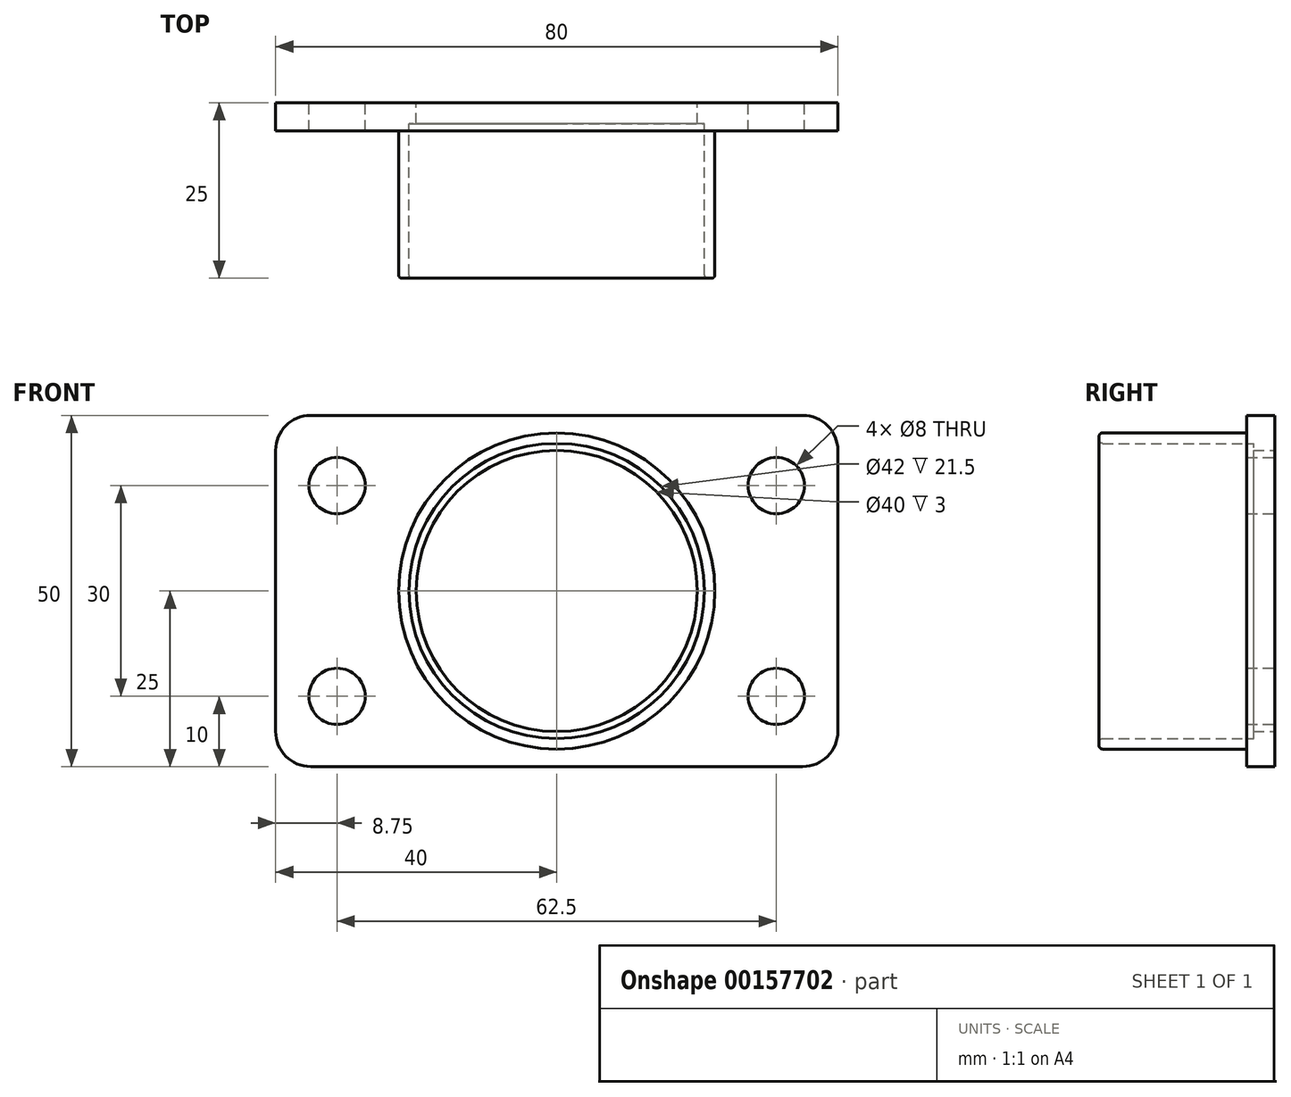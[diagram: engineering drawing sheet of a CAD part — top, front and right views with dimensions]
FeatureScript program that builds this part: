
annotation { "Feature Type Name" : "Feature", "Feature Type Description" : "" }
export const myFeature = defineFeature(function(context is Context, id is Id, definition is map)
    precondition{}
    {
        {
            var Q0;
            Q0=qCreatedBy(makeId("Front.planeOp"),FACE);
            var sketch = newSketch(context, id + "F0", { "sketchPlane" : qUnion([Q0])});
            skLineSegment(sketch, "E0.bottom", {"start": v(-40, 25) * mm, "end": v(40, 25) * mm});
            skLineSegment(sketch, "E0.top", {"start": v(-40, -25) * mm, "end": v(40, -25) * mm});
            skLineSegment(sketch, "E0.left", {"start": v(-40, 25) * mm, "end": v(-40, -25) * mm});
            skLineSegment(sketch, "E0.right", {"start": v(40, 25) * mm, "end": v(40, -25) * mm});
            skPoint(sketch, "E0.middle", {"position": v(0, 0) * mm});
            skCircle(sketch, "E1", {"center": v(0, 0) * mm, "radius": 22.5 * mm});
            skCircle(sketch, "E2", {"center": v(0, 0) * mm, "radius": 21 * mm});
            skLineSegment(sketch, "E3", {"start": v(-40, 0) * mm, "end": v(-31.25, 0) * mm});
            skPoint(sketch, "E3.endSnap0", {"position": v(-40, 0) * mm});
            skLineSegment(sketch, "E4", {"start": v(40, 0) * mm, "end": v(31.25, 0) * mm});
            skLineSegment(sketch, "E5", {"start": v(-31.25, 0) * mm, "end": v(-31.25, 15) * mm});
            skLineSegment(sketch, "E6", {"start": v(-31.25, 0) * mm, "end": v(-31.25, -15) * mm});
            skLineSegment(sketch, "E7", {"start": v(31.25, 0) * mm, "end": v(31.25, 15) * mm});
            skLineSegment(sketch, "E8", {"start": v(31.25, 0) * mm, "end": v(31.25, -15) * mm});
            skCircle(sketch, "E9", {"center": v(-31.25, 15) * mm, "radius": 4 * mm});
            skCircle(sketch, "E10", {"center": v(-31.25, -15) * mm, "radius": 4 * mm});
            skCircle(sketch, "E11", {"center": v(31.25, 15) * mm, "radius": 4 * mm});
            skCircle(sketch, "E12", {"center": v(31.25, -15) * mm, "radius": 4 * mm});
            skCircle(sketch, "E13", {"center": v(0, 0) * mm, "radius": 20 * mm});
            skSolve(sketch);
        }
        {
            var Q0;
            {var subQ3=sQuery(id+"F0.wireOp",EDGE,"E0.bottom");Q0=makeQuery(id+"F0.imprint","IMPRINT",FACE,{"disambiguationData":[TD([[makeQuery(id+"F0.imprint","IMPRINT",EDGE,{"derivedFrom":subQ3}),-1.0]])]});}
            extrude(context, id + "F1", {"entities" : qUnion([Q0]), "depth" : 4 * mm});
        }
        {
            var Q0;
            Q0=makeQuery(id+"F0.imprint","IMPRINT",FACE,{"disambiguationData":[TD([[makeQuery(id+"F0.imprint","IMPRINT",EDGE,{"derivedFrom":sQuery(id+"F0.wireOp",EDGE,"E1")}),1.0]])]});
            extrude(context, id + "F2", {"entities" : qUnion([Q0]), "operationType" : NewBodyOperationType.ADD, "depth" : 25 * mm});
        }
        {
            var Q0;
            Q0=makeQuery(id+"F1.opExtrude","SWEPT_EDGE",EDGE,{"disambiguationData":[OSD([sQuery(id+"F0.wireOp",EDGE,"E0.top"),sQuery(id+"F0.wireOp",EDGE,"E0.left")])]});
            var Q1;
            Q1=makeQuery(id+"F1.opExtrude","SWEPT_EDGE",EDGE,{"disambiguationData":[OSD([sQuery(id+"F0.wireOp",EDGE,"E0.bottom"),sQuery(id+"F0.wireOp",EDGE,"E0.left")])]});
            var Q2;
            Q2=makeQuery(id+"F1.opExtrude","SWEPT_EDGE",EDGE,{"disambiguationData":[OSD([sQuery(id+"F0.wireOp",EDGE,"E0.bottom"),sQuery(id+"F0.wireOp",EDGE,"E0.right")])]});
            var Q3;
            Q3=makeQuery(id+"F1.opExtrude","SWEPT_EDGE",EDGE,{"disambiguationData":[OSD([sQuery(id+"F0.wireOp",EDGE,"E0.top"),sQuery(id+"F0.wireOp",EDGE,"E0.right")])]});
            fillet(context, id + "F3", {"entities" : qUnion([Q0, Q1, Q2, Q3]), "radius" : 5 * mm, "tangentPropagation" : true, "allowEdgeOverflow" : false});
        }
        {
            var Q0;
            Q0=makeQuery(id+"F2.opExtrude","CAP_EDGE",EDGE,{"disambiguationData":[OSD([sQuery(id+"F0.wireOp",EDGE,"E1")])],"isStart":false});
            var Q1;
            Q1=makeQuery(id+"F2.opExtrude","CAP_EDGE",EDGE,{"disambiguationData":[OSD([sQuery(id+"F0.wireOp",EDGE,"E2")])],"isStart":false});
            fillet(context, id + "F4", {"entities" : qUnion([Q0, Q1]), "radius" : 0.5 * mm, "tangentPropagation" : true, "allowEdgeOverflow" : false});
        }
        {
            var Q0;
            Q0=makeQuery(id+"F0.imprint","IMPRINT",FACE,{"disambiguationData":[TD([[makeQuery(id+"F0.imprint","IMPRINT",EDGE,{"derivedFrom":sQuery(id+"F0.wireOp",EDGE,"E2")}),1.0]])]});
            extrude(context, id + "F5", {"entities" : qUnion([Q0]), "operationType" : NewBodyOperationType.ADD, "depth" : 3 * mm});
        }
    });
